# Revit family: CAME_Термосканер_СистемКонтроля_SEP-FRTMP01
name_source: partatom
category: Специальное оборудование
units: mm (PartAtom-declared; Revit-internal decimal feet)

## family parameters
Всегда вертикально = Да
На основе рабочей плоскости = Нет
Общий = Нет
При загрузке вырезать с полостями = Нет
Размер круглого соединителя = Использовать диаметр
Тип детали = Нормальный
Точка расчета площади = Нет

## types (1)
- CAME_Термосканер_СистемКонтроля_SEP-FRTMP01
    ADSK_URL документации изделия = https://camerussia.com
    ADSK_URL страницы изделия = https://camerussia.com
    ADSK_Версия Revit = 2019
    ADSK_Версия семейства = 1.0
    ADSK_Группирование = Термосканер
    ADSK_Единица измерения = шт.
    ADSK_Завод-изготовитель = CAME
    ADSK_Классификация нагрузок = Прочее
    ADSK_Код изделия = Код КСР 26.30.50.119.61.2.07.09
    ADSK_Количество = 1
    ADSK_Количество фаз = 1
    ADSK_Коэффициент мощности = 0.96
    ADSK_Марка = АРТ:815XC-0010
    ADSK_Масса = 1.66
    ADSK_Масса_Текст = 1.66 кг
    ADSK_Наименование = Термосканер SEP-FRTMP01 для систем контроля доступа с функцией контроля наличия маски
    ADSK_Наименование краткое = Термосканер SEP-FRTMP01
    ADSK_Напряжение = 12 В
    ADSK_Номинальная мощность = 12 Вт
    ADSK_Обозначение = ТУ 26.30.50-001-89603926-2021
    ADSK_Полная мощность = 13 В·А
    ADSK_Размер_Высота = 302 мм
    ADSK_Размер_Глубина = 34 мм
    ADSK_Размер_Ширина = 139 мм
    BL_BIM library = https://bimlib.pro
    CAME_Диапазон рабочих температур (°C) = -0 ÷ +40
    URL = https://camerussia.com
    Группа модели = Турникеты
    Изготовитель = CAME
    Описание = Термосканер для систем контроля доступа. Многофункциональный терминал с 8-дюймовым дисплеем с функциями измерения температуры, распознавания лиц и контроля наличия маски. Ёмкость хранения: 20 000 лиц. Время распознавания лица: 0,5 с. Материал: Пластик, текстолит, алюминий.
